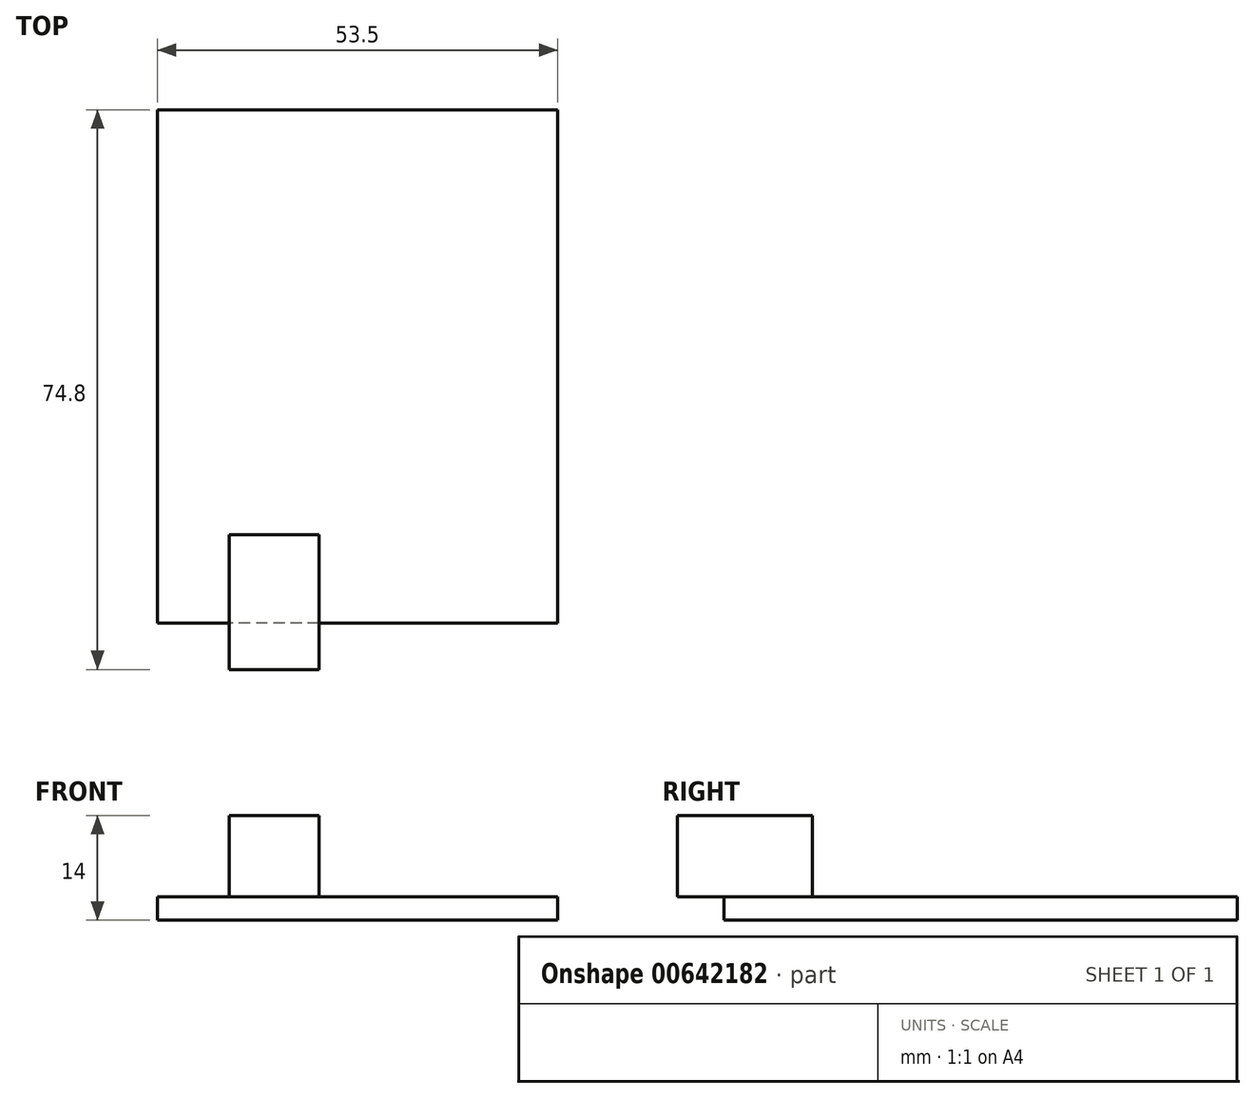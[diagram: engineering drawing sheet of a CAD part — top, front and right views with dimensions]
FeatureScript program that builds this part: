
annotation { "Feature Type Name" : "Feature", "Feature Type Description" : "" }
export const myFeature = defineFeature(function(context is Context, id is Id, definition is map)
    precondition{}
    {
        {
            var Q0;
            Q0=qCreatedBy(makeId("Top.planeOp"),FACE);
            var sketch = newSketch(context, id + "F0", { "sketchPlane" : qUnion([Q0])});
            skLineSegment(sketch, "E0.bottom", {"start": v(26.75, -34.3) * mm, "end": v(-26.75, -34.3) * mm});
            skLineSegment(sketch, "E0.top", {"start": v(26.75, 34.3) * mm, "end": v(-26.75, 34.3) * mm});
            skLineSegment(sketch, "E0.left", {"start": v(26.75, -34.3) * mm, "end": v(26.75, 34.3) * mm});
            skLineSegment(sketch, "E0.right", {"start": v(-26.75, -34.3) * mm, "end": v(-26.75, 34.3) * mm});
            skPoint(sketch, "E0.middle", {"position": v(0, 0) * mm});
            skSolve(sketch);
        }
        {
            var Q0;
            Q0 = qSketchRegion(id + "F0", true);
            extrude(context, id + "F1", {"entities" : qUnion([Q0]), "oppositeDirection" : true, "depth" : 3.1 * mm, "offsetDistance" : 25.4 * mm});
        }
        {
            var Q0;
            Q0=qCreatedBy(makeId("Top.planeOp"),FACE);
            var sketch = newSketch(context, id + "F2", { "sketchPlane" : qUnion([Q0])});
            skLineSegment(sketch, "E1.bottom", {"start": v(-5.15, -40.5) * mm, "end": v(-17.15, -40.5) * mm});
            skLineSegment(sketch, "E1.top", {"start": v(-5.15, -22.5) * mm, "end": v(-17.15, -22.5) * mm});
            skLineSegment(sketch, "E1.left", {"start": v(-5.15, -40.5) * mm, "end": v(-5.15, -22.5) * mm});
            skLineSegment(sketch, "E1.right", {"start": v(-17.15, -40.5) * mm, "end": v(-17.15, -22.5) * mm});
            skSolve(sketch);
        }
        {
            var Q0;
            Q0 = qSketchRegion(id + "F2", true);
            extrude(context, id + "F3", {"entities" : qUnion([Q0]), "operationType" : NewBodyOperationType.ADD, "depth" : 10.9 * mm, "offsetDistance" : 25.4 * mm});
        }
    });
